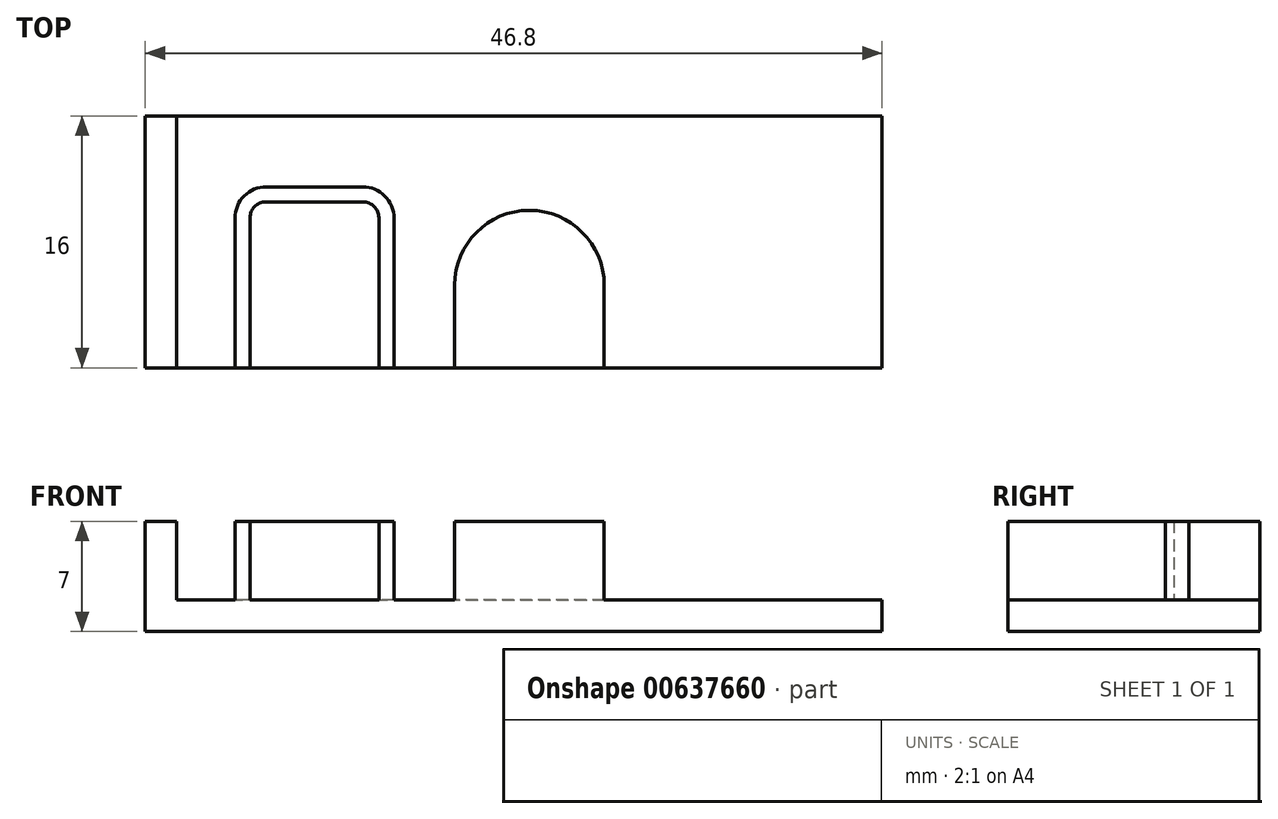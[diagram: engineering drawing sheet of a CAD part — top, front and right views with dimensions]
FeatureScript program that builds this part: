
annotation { "Feature Type Name" : "Feature", "Feature Type Description" : "" }
export const myFeature = defineFeature(function(context is Context, id is Id, definition is map)
    precondition{}
    {
        {
            var Q0;
            Q0=qCreatedBy(makeId("Top.planeOp"),FACE);
            var sketch = newSketch(context, id + "F0", { "sketchPlane" : qUnion([Q0])});
            skLineSegment(sketch, "E0.bottom", {"start": v(-22.4, -8) * mm, "end": v(22.4, -8) * mm});
            skLineSegment(sketch, "E0.top", {"start": v(-22.4, 8) * mm, "end": v(22.4, 8) * mm});
            skLineSegment(sketch, "E0.left", {"start": v(-22.4, -8) * mm, "end": v(-22.4, 8) * mm});
            skLineSegment(sketch, "E0.right", {"start": v(22.4, -8) * mm, "end": v(22.4, 8) * mm});
            skSolve(sketch);
        }
        {
            var Q0;
            Q0=qSketchRegion(id+"F0",true);
            extrude(context, id + "F1", {"entities" : qUnion([Q0]), "depth" : 2 * mm, "offsetDistance" : 25 * mm});
        }
        {
            var Q0;
            Q0=makeQuery(id+"F1.opExtrude","CAP_FACE",FACE,{"disambiguationData":[OSD([sQuery(id+"F0.wireOp",EDGE,"E0.bottom"),sQuery(id+"F0.wireOp",EDGE,"E0.top"),sQuery(id+"F0.wireOp",EDGE,"E0.left"),sQuery(id+"F0.wireOp",EDGE,"E0.right")])],"isStart":false});
            var sketch = newSketch(context, id + "F2", { "sketchPlane" : qUnion([Q0])});
            skLineSegment(sketch, "E1.0", {"start": v(-22.4, -8) * mm, "end": v(22.4, -8) * mm, "construction": true});
            skLineSegment(sketch, "E1.1", {"start": v(-22.4, -8) * mm, "end": v(-22.4, 8) * mm, "construction": true});
            skLineSegment(sketch, "E2", {"start": v(-18.7, -8) * mm, "end": v(-18.7, 1.5) * mm});
            skLineSegment(sketch, "E3", {"start": v(-16.7, 3.5) * mm, "end": v(-10.6, 3.5) * mm});
            skLineSegment(sketch, "E4", {"start": v(-8.6, 1.5) * mm, "end": v(-8.6, -8) * mm});
            skLineSegment(sketch, "E5.0", {"start": v(-9.56, 1.54) * mm, "end": v(-9.56, -8) * mm});
            skLineSegment(sketch, "E5.1", {"start": v(-16.74, 2.54) * mm, "end": v(-10.56, 2.54) * mm});
            skLineSegment(sketch, "E5.2", {"start": v(-17.74, -8) * mm, "end": v(-17.74, 1.54) * mm});
            skLineSegment(sketch, "E6", {"start": v(-18.7, -8) * mm, "end": v(-17.74, -8) * mm});
            skLineSegment(sketch, "E7", {"start": v(-9.56, -8) * mm, "end": v(-8.6, -8) * mm});
            skPoint(sketch, "E8.visualSharp", {"position": v(-17.74, 2.54) * mm});
            skArc(sketch, "E8.filletArc", {"start": v(-16.74, 2.54) * mm, "mid": v(-17.45, 2.25) * mm, "end": v(-17.74, 1.54) * mm});
            skPoint(sketch, "E9.visualSharp", {"position": v(-9.56, 2.54) * mm});
            skArc(sketch, "E9.filletArc", {"start": v(-9.56, 1.54) * mm, "mid": v(-9.85, 2.25) * mm, "end": v(-10.56, 2.54) * mm});
            skPoint(sketch, "E10.visualSharp", {"position": v(-18.7, 3.5) * mm});
            skArc(sketch, "E10.filletArc", {"start": v(-16.7, 3.5) * mm, "mid": v(-18.11, 2.91) * mm, "end": v(-18.7, 1.5) * mm});
            skPoint(sketch, "E11.visualSharp", {"position": v(-8.6, 3.5) * mm});
            skArc(sketch, "E11.filletArc", {"start": v(-8.6, 1.5) * mm, "mid": v(-9.19, 2.91) * mm, "end": v(-10.6, 3.5) * mm});
            skSolve(sketch);
        }
        {
            var Q0;
            {var subQ3=sQuery(id+"F2.wireOp",EDGE,"E2");Q0=makeQuery(id+"F2.imprint","IMPRINT",FACE,{"disambiguationData":[TD([[makeQuery(id+"F2.imprint","IMPRINT",EDGE,{"derivedFrom":subQ3}),1.0]])]});}
            var sketch = newSketch(context, id + "F3", { "sketchPlane" : qUnion([Q0])});
            skArc(sketch, "E12", {"start": v(4.75, -2.75) * mm, "mid": v(0, 2) * mm, "end": v(-4.75, -2.75) * mm});
            skLineSegment(sketch, "E13.0", {"start": v(-22.4, -8) * mm, "end": v(22.4, -8) * mm, "construction": true});
            skLineSegment(sketch, "E14", {"start": v(-4.75, -8) * mm, "end": v(-4.75, -2.75) * mm});
            skLineSegment(sketch, "E15.MirrorCS", {"start": v(4.75, -8) * mm, "end": v(4.75, -2.75) * mm});
            skLineSegment(sketch, "E16", {"start": v(-4.75, -8) * mm, "end": v(4.75, -8) * mm});
            skSolve(sketch);
        }
        {
            var Q0;
            Q0=makeQuery(id+"F2.imprint","IMPRINT",FACE,{"disambiguationData":[TD([[makeQuery(id+"F2.imprint","IMPRINT",EDGE,{"derivedFrom":sQuery(id+"F2.wireOp",EDGE,"E2")}),-1.0]])]});
            extrude(context, id + "F4", {"entities" : qUnion([Q0]), "operationType" : NewBodyOperationType.ADD, "depth" : 5 * mm, "offsetDistance" : 25 * mm});
        }
        {
            var Q0;
            Q0=makeQuery(id+"F3.imprint","IMPRINT",FACE,{"disambiguationData":[TD([[makeQuery(id+"F3.imprint","IMPRINT",EDGE,{"derivedFrom":sQuery(id+"F3.wireOp",EDGE,"E12")}),1.0]])]});
            extrude(context, id + "F5", {"entities" : qUnion([Q0]), "operationType" : NewBodyOperationType.ADD, "depth" : 5 * mm, "offsetDistance" : 25 * mm});
        }
        {
            var Q0;
            Q0=qCreatedBy(makeId("Top.planeOp"),FACE);
            var sketch = newSketch(context, id + "F6", { "sketchPlane" : qUnion([Q0])});
            skLineSegment(sketch, "E17.0", {"start": v(-22.4, -8) * mm, "end": v(-22.4, 8) * mm});
            skLineSegment(sketch, "E18", {"start": v(-22.4, -8) * mm, "end": v(-24.4, -8) * mm});
            skLineSegment(sketch, "E19", {"start": v(-24.4, -8) * mm, "end": v(-24.4, 8) * mm});
            skLineSegment(sketch, "E20", {"start": v(-24.4, 8) * mm, "end": v(-22.4, 8) * mm});
            skSolve(sketch);
        }
        {
            var Q0;
            Q0=makeQuery(id+"F6.imprint","IMPRINT",FACE,{"disambiguationData":[TD([[makeQuery(id+"F6.imprint","IMPRINT",EDGE,{"derivedFrom":sQuery(id+"F6.wireOp",EDGE,"E17.0")}),1.0]])]});
            var Q1;
            Q1=makeQuery(id+"F4.opExtrude","CAP_FACE",FACE,{"disambiguationData":[OSD([sQuery(id+"F2.wireOp",EDGE,"E2"),sQuery(id+"F2.wireOp",EDGE,"E3"),sQuery(id+"F2.wireOp",EDGE,"E4"),sQuery(id+"F2.wireOp",EDGE,"E5.0"),sQuery(id+"F2.wireOp",EDGE,"E5.1"),sQuery(id+"F2.wireOp",EDGE,"E5.2"),sQuery(id+"F2.wireOp",EDGE,"E6"),sQuery(id+"F2.wireOp",EDGE,"E7"),sQuery(id+"F2.wireOp",EDGE,"E8.filletArc"),sQuery(id+"F2.wireOp",EDGE,"E9.filletArc"),sQuery(id+"F2.wireOp",EDGE,"E10.filletArc"),sQuery(id+"F2.wireOp",EDGE,"E11.filletArc")])],"isStart":false});
            extrude(context, id + "F7", {"entities" : qUnion([Q0]), "operationType" : NewBodyOperationType.ADD, "endBound" : BoundingType.UP_TO_SURFACE, "depth" : 25 * mm, "endBoundEntityFace" : qUnion([Q1]), "offsetDistance" : 25 * mm});
        }
    });
